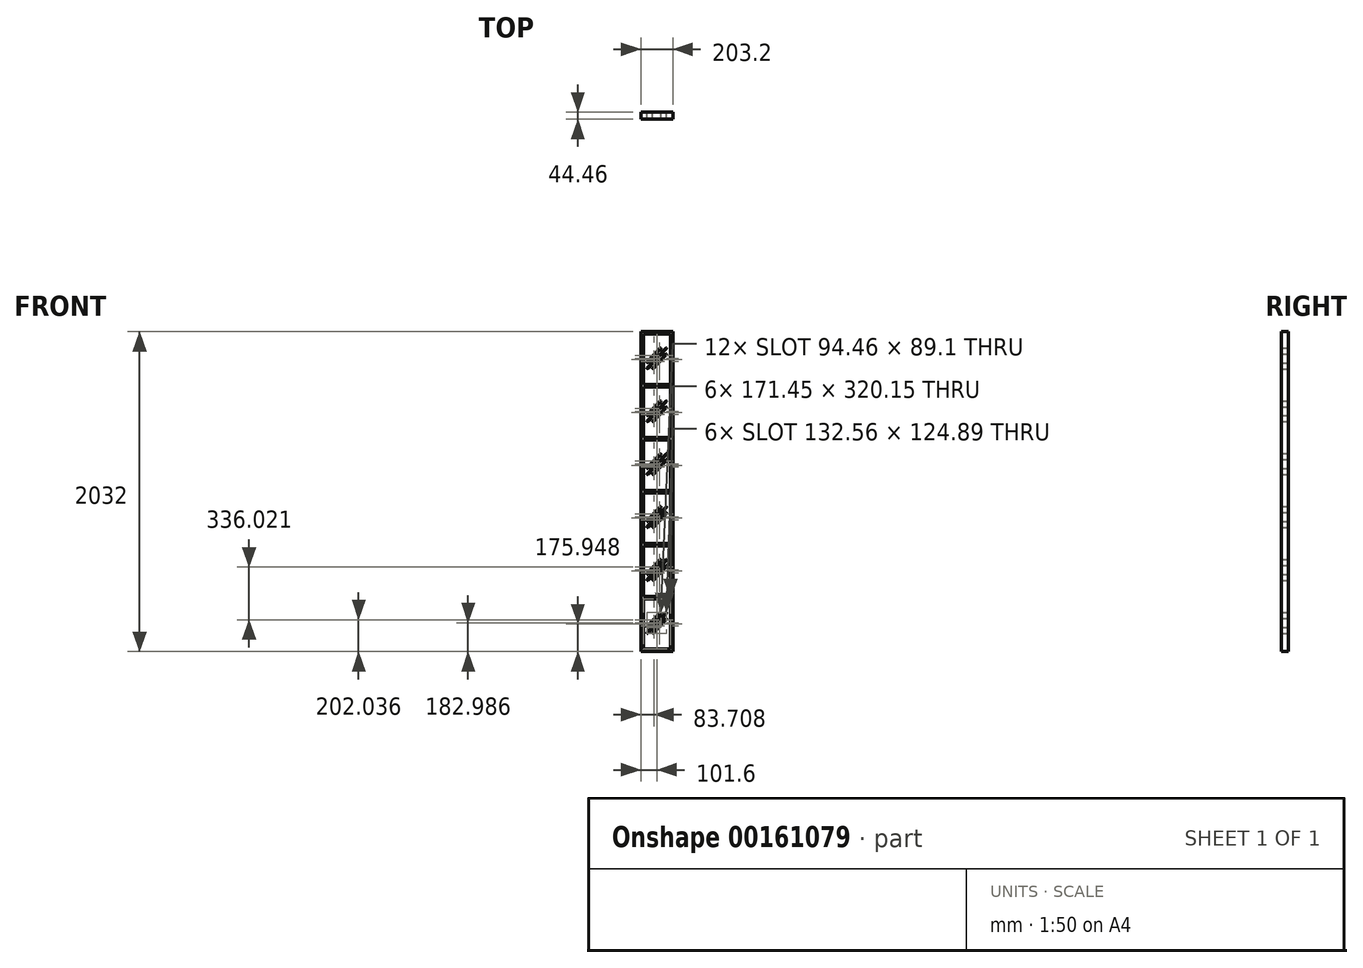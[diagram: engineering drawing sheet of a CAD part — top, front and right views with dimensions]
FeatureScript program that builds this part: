
annotation { "Feature Type Name" : "Feature", "Feature Type Description" : "" }
export const myFeature = defineFeature(function(context is Context, id is Id, definition is map)
    precondition{}
    {
        {
            var Q0;
            Q0=qCreatedBy(makeId("Front.planeOp"),FACE);
            var sketch = newSketch(context, id + "F0", { "sketchPlane" : qUnion([Q0])});
            skLineSegment(sketch, "E0.bottom", {"start": v(0, 0) * mm, "end": v(203.2, 0) * mm});
            skLineSegment(sketch, "E0.top", {"start": v(0, 2032) * mm, "end": v(203.2, 2032) * mm});
            skLineSegment(sketch, "E0.left", {"start": v(0, 0) * mm, "end": v(0, 2032) * mm});
            skLineSegment(sketch, "E0.right", {"start": v(203.2, 0) * mm, "end": v(203.2, 2032) * mm});
            skLineSegment(sketch, "E1.bottom", {"start": v(15.88, 15.88) * mm, "end": v(187.33, 15.88) * mm});
            skLineSegment(sketch, "E1.top", {"start": v(15.88, 336.02) * mm, "end": v(187.33, 336.02) * mm});
            skLineSegment(sketch, "E1.left", {"start": v(15.88, 15.88) * mm, "end": v(15.88, 336.02) * mm});
            skLineSegment(sketch, "E1.right", {"start": v(187.32, 15.88) * mm, "end": v(187.32, 336.02) * mm});
            skLineSegment(sketch, "E2.bottom", {"start": v(187.32, 351.9) * mm, "end": v(15.88, 351.9) * mm});
            skLineSegment(sketch, "E2.top", {"start": v(187.32, 672.04) * mm, "end": v(15.88, 672.04) * mm});
            skLineSegment(sketch, "E2.left", {"start": v(187.32, 351.9) * mm, "end": v(187.32, 672.04) * mm});
            skLineSegment(sketch, "E2.right", {"start": v(15.88, 351.9) * mm, "end": v(15.88, 672.04) * mm});
            skLineSegment(sketch, "E3.bottom", {"start": v(187.32, 687.92) * mm, "end": v(15.88, 687.92) * mm});
            skLineSegment(sketch, "E3.top", {"start": v(187.32, 1008.06) * mm, "end": v(15.88, 1008.06) * mm});
            skLineSegment(sketch, "E3.left", {"start": v(187.32, 687.92) * mm, "end": v(187.32, 1008.06) * mm});
            skLineSegment(sketch, "E3.right", {"start": v(15.88, 687.92) * mm, "end": v(15.87, 1008.06) * mm});
            skLineSegment(sketch, "E4.bottom", {"start": v(187.32, 1023.94) * mm, "end": v(15.88, 1023.94) * mm});
            skLineSegment(sketch, "E4.top", {"start": v(187.33, 1344.08) * mm, "end": v(15.87, 1344.08) * mm});
            skLineSegment(sketch, "E4.left", {"start": v(187.32, 1023.94) * mm, "end": v(187.32, 1344.08) * mm});
            skLineSegment(sketch, "E4.right", {"start": v(15.88, 1023.94) * mm, "end": v(15.87, 1344.08) * mm});
            skLineSegment(sketch, "E5.bottom", {"start": v(187.33, 1359.96) * mm, "end": v(15.87, 1359.96) * mm});
            skLineSegment(sketch, "E5.top", {"start": v(187.32, 1680.1) * mm, "end": v(15.87, 1680.1) * mm});
            skLineSegment(sketch, "E5.left", {"start": v(187.32, 1359.96) * mm, "end": v(187.32, 1680.1) * mm});
            skLineSegment(sketch, "E5.right", {"start": v(15.87, 1359.96) * mm, "end": v(15.87, 1680.1) * mm});
            skLineSegment(sketch, "E6.bottom", {"start": v(187.33, 1695.98) * mm, "end": v(15.87, 1695.98) * mm});
            skLineSegment(sketch, "E6.top", {"start": v(187.33, 2016.13) * mm, "end": v(15.87, 2016.13) * mm});
            skLineSegment(sketch, "E6.left", {"start": v(187.32, 1695.98) * mm, "end": v(187.32, 2016.13) * mm});
            skLineSegment(sketch, "E6.right", {"start": v(15.87, 1695.98) * mm, "end": v(15.87, 2016.13) * mm});
            skSolve(sketch);
        }
        {
            var Q0;
            Q0=qSketchRegion(id+"F0",true);
            extrude(context, id + "F1", {"entities" : qUnion([Q0]), "depth" : 22.22 * mm, "hasSecondDirection" : true, "secondDirectionOppositeDirection" : true, "secondDirectionDepth" : 22.22 * mm});
        }
        {
            var Q0;
            Q0=qCreatedBy(makeId("Front.planeOp"),FACE);
            var sketch = newSketch(context, id + "F2", { "sketchPlane" : qUnion([Q0])});
            skLineSegment(sketch, "E7.0", {"start": v(187.32, 1680.1) * mm, "end": v(15.87, 1680.1) * mm});
            skLineSegment(sketch, "E8.0", {"start": v(15.87, 1359.96) * mm, "end": v(15.87, 1680.1) * mm});
            skLineSegment(sketch, "E9.0", {"start": v(187.32, 1359.96) * mm, "end": v(15.87, 1359.96) * mm});
            skLineSegment(sketch, "E10.0", {"start": v(187.32, 1359.96) * mm, "end": v(187.32, 1680.1) * mm});
            skLineSegment(sketch, "E11.0", {"start": v(187.32, 1023.94) * mm, "end": v(187.32, 1344.08) * mm});
            skLineSegment(sketch, "E12.0", {"start": v(187.32, 1344.08) * mm, "end": v(15.87, 1344.08) * mm});
            skLineSegment(sketch, "E13.0", {"start": v(15.88, 1023.94) * mm, "end": v(15.87, 1344.08) * mm});
            skLineSegment(sketch, "E14.0", {"start": v(187.32, 1023.94) * mm, "end": v(15.88, 1023.94) * mm});
            skLineSegment(sketch, "E15.0", {"start": v(187.32, 1008.06) * mm, "end": v(15.88, 1008.06) * mm});
            skLineSegment(sketch, "E16.0", {"start": v(15.88, 687.92) * mm, "end": v(15.87, 1008.06) * mm});
            skLineSegment(sketch, "E17.0", {"start": v(187.32, 687.92) * mm, "end": v(187.32, 1008.06) * mm});
            skLineSegment(sketch, "E18.0", {"start": v(187.32, 687.92) * mm, "end": v(15.88, 687.92) * mm});
            skLineSegment(sketch, "E19.0", {"start": v(187.32, 351.9) * mm, "end": v(187.32, 672.04) * mm});
            skLineSegment(sketch, "E20.0", {"start": v(187.32, 351.9) * mm, "end": v(15.88, 351.9) * mm});
            skLineSegment(sketch, "E21.0", {"start": v(187.32, 672.04) * mm, "end": v(15.88, 672.04) * mm});
            skLineSegment(sketch, "E22.0", {"start": v(15.88, 351.9) * mm, "end": v(15.88, 672.04) * mm});
            skLineSegment(sketch, "E23.0", {"start": v(15.88, 336.02) * mm, "end": v(187.32, 336.02) * mm});
            skLineSegment(sketch, "E24.0", {"start": v(15.88, 15.88) * mm, "end": v(15.88, 336.02) * mm});
            skLineSegment(sketch, "E25.0", {"start": v(187.32, 15.88) * mm, "end": v(187.32, 336.02) * mm});
            skLineSegment(sketch, "E26.0", {"start": v(15.88, 15.88) * mm, "end": v(187.32, 15.88) * mm});
            skLineSegment(sketch, "E27", {"start": v(160.87, 246.1) * mm, "end": v(42.33, 119.88) * mm});
            skLineSegment(sketch, "E28", {"start": v(160.87, 208) * mm, "end": v(78.11, 119.88) * mm});
            skLineSegment(sketch, "E29", {"start": v(125.09, 246.1) * mm, "end": v(42.33, 157.98) * mm});
            skArc(sketch, "E30.0.startCap", {"start": v(122.77, 248.27) * mm, "mid": v(127.26, 248.4) * mm, "end": v(127.4, 243.92) * mm});
            skArc(sketch, "E30.0.endCap", {"start": v(44.64, 155.8) * mm, "mid": v(40.16, 155.67) * mm, "end": v(40.01, 160.15) * mm});
            skLineSegment(sketch, "E30.0.left", {"start": v(127.4, 243.92) * mm, "end": v(44.64, 155.8) * mm});
            skLineSegment(sketch, "E30.0.right", {"start": v(122.77, 248.27) * mm, "end": v(40.01, 160.15) * mm});
            skArc(sketch, "E30.1.startCap", {"start": v(158.56, 248.27) * mm, "mid": v(163.04, 248.4) * mm, "end": v(163.19, 243.92) * mm});
            skArc(sketch, "E30.1.endCap", {"start": v(44.64, 117.7) * mm, "mid": v(40.16, 117.57) * mm, "end": v(40.01, 122.05) * mm});
            skLineSegment(sketch, "E30.1.left", {"start": v(163.19, 243.92) * mm, "end": v(44.64, 117.7) * mm});
            skLineSegment(sketch, "E30.1.right", {"start": v(158.56, 248.27) * mm, "end": v(40.01, 122.05) * mm});
            skArc(sketch, "E30.2.startCap", {"start": v(158.56, 210.17) * mm, "mid": v(163.04, 210.3) * mm, "end": v(163.19, 205.82) * mm});
            skArc(sketch, "E30.2.endCap", {"start": v(80.43, 117.7) * mm, "mid": v(75.94, 117.57) * mm, "end": v(75.8, 122.05) * mm});
            skLineSegment(sketch, "E30.2.left", {"start": v(163.19, 205.82) * mm, "end": v(80.43, 117.7) * mm});
            skLineSegment(sketch, "E30.2.right", {"start": v(158.56, 210.17) * mm, "end": v(75.8, 122.05) * mm});
            skLineSegment(sketch, "E31.0.1.0", {"start": v(160.87, 582.11) * mm, "end": v(42.33, 455.9) * mm});
            skLineSegment(sketch, "E31.0.1.1", {"start": v(158.56, 546.19) * mm, "end": v(75.8, 458.07) * mm});
            skLineSegment(sketch, "E31.0.1.2", {"start": v(163.19, 579.94) * mm, "end": v(44.64, 453.73) * mm});
            skLineSegment(sketch, "E31.0.1.3", {"start": v(122.77, 584.29) * mm, "end": v(40.01, 496.17) * mm});
            skLineSegment(sketch, "E31.0.1.4", {"start": v(163.19, 541.84) * mm, "end": v(80.43, 453.73) * mm});
            skLineSegment(sketch, "E31.0.1.5", {"start": v(127.4, 579.94) * mm, "end": v(44.64, 491.83) * mm});
            skLineSegment(sketch, "E31.0.1.6", {"start": v(160.87, 544.01) * mm, "end": v(78.11, 455.9) * mm});
            skLineSegment(sketch, "E31.0.1.7", {"start": v(125.09, 582.11) * mm, "end": v(42.33, 494) * mm});
            skLineSegment(sketch, "E31.0.1.8", {"start": v(158.56, 584.29) * mm, "end": v(40.01, 458.07) * mm});
            skArc(sketch, "E31.0.1.9", {"start": v(122.77, 584.29) * mm, "mid": v(127.26, 584.43) * mm, "end": v(127.4, 579.94) * mm});
            skArc(sketch, "E31.0.1.10", {"start": v(158.56, 584.29) * mm, "mid": v(163.04, 584.43) * mm, "end": v(163.19, 579.94) * mm});
            skArc(sketch, "E31.0.1.11", {"start": v(44.64, 453.73) * mm, "mid": v(40.16, 453.59) * mm, "end": v(40.01, 458.07) * mm});
            skArc(sketch, "E31.0.1.12", {"start": v(44.64, 491.83) * mm, "mid": v(40.16, 491.69) * mm, "end": v(40.01, 496.17) * mm});
            skArc(sketch, "E31.0.1.13", {"start": v(80.43, 453.73) * mm, "mid": v(75.94, 453.59) * mm, "end": v(75.8, 458.07) * mm});
            skArc(sketch, "E31.0.1.14", {"start": v(158.56, 546.19) * mm, "mid": v(163.04, 546.33) * mm, "end": v(163.19, 541.84) * mm});
            skLineSegment(sketch, "E31.0.2.0", {"start": v(160.87, 918.13) * mm, "end": v(42.33, 791.92) * mm});
            skLineSegment(sketch, "E31.0.2.1", {"start": v(158.56, 882.2) * mm, "end": v(75.8, 794.1) * mm});
            skLineSegment(sketch, "E31.0.2.2", {"start": v(163.19, 915.96) * mm, "end": v(44.64, 789.75) * mm});
            skLineSegment(sketch, "E31.0.2.3", {"start": v(122.77, 920.3) * mm, "end": v(40.01, 832.2) * mm});
            skLineSegment(sketch, "E31.0.2.4", {"start": v(163.19, 877.86) * mm, "end": v(80.43, 789.75) * mm});
            skLineSegment(sketch, "E31.0.2.5", {"start": v(127.4, 915.96) * mm, "end": v(44.64, 827.85) * mm});
            skLineSegment(sketch, "E31.0.2.6", {"start": v(160.87, 880.03) * mm, "end": v(78.11, 791.92) * mm});
            skLineSegment(sketch, "E31.0.2.7", {"start": v(125.09, 918.13) * mm, "end": v(42.33, 830.02) * mm});
            skLineSegment(sketch, "E31.0.2.8", {"start": v(158.56, 920.3) * mm, "end": v(40.01, 794.1) * mm});
            skArc(sketch, "E31.0.2.9", {"start": v(122.77, 920.3) * mm, "mid": v(127.26, 920.45) * mm, "end": v(127.4, 915.96) * mm});
            skArc(sketch, "E31.0.2.10", {"start": v(158.56, 920.3) * mm, "mid": v(163.04, 920.45) * mm, "end": v(163.19, 915.96) * mm});
            skArc(sketch, "E31.0.2.11", {"start": v(44.64, 789.75) * mm, "mid": v(40.16, 789.6) * mm, "end": v(40.01, 794.1) * mm});
            skArc(sketch, "E31.0.2.12", {"start": v(44.64, 827.85) * mm, "mid": v(40.16, 827.7) * mm, "end": v(40.01, 832.2) * mm});
            skArc(sketch, "E31.0.2.13", {"start": v(80.43, 789.75) * mm, "mid": v(75.94, 789.6) * mm, "end": v(75.8, 794.1) * mm});
            skArc(sketch, "E31.0.2.14", {"start": v(158.56, 882.2) * mm, "mid": v(163.04, 882.35) * mm, "end": v(163.19, 877.86) * mm});
            skLineSegment(sketch, "E31.0.3.0", {"start": v(160.87, 1254.15) * mm, "end": v(42.33, 1127.94) * mm});
            skLineSegment(sketch, "E31.0.3.1", {"start": v(158.56, 1218.23) * mm, "end": v(75.8, 1130.12) * mm});
            skLineSegment(sketch, "E31.0.3.2", {"start": v(163.19, 1251.98) * mm, "end": v(44.64, 1125.77) * mm});
            skLineSegment(sketch, "E31.0.3.3", {"start": v(122.77, 1256.33) * mm, "end": v(40.01, 1168.22) * mm});
            skLineSegment(sketch, "E31.0.3.4", {"start": v(163.19, 1213.88) * mm, "end": v(80.43, 1125.77) * mm});
            skLineSegment(sketch, "E31.0.3.5", {"start": v(127.4, 1251.98) * mm, "end": v(44.64, 1163.87) * mm});
            skLineSegment(sketch, "E31.0.3.6", {"start": v(160.87, 1216.05) * mm, "end": v(78.11, 1127.94) * mm});
            skLineSegment(sketch, "E31.0.3.7", {"start": v(125.09, 1254.15) * mm, "end": v(42.33, 1166.04) * mm});
            skLineSegment(sketch, "E31.0.3.8", {"start": v(158.56, 1256.33) * mm, "end": v(40.01, 1130.12) * mm});
            skArc(sketch, "E31.0.3.9", {"start": v(122.77, 1256.33) * mm, "mid": v(127.26, 1256.47) * mm, "end": v(127.4, 1251.98) * mm});
            skArc(sketch, "E31.0.3.10", {"start": v(158.56, 1256.33) * mm, "mid": v(163.04, 1256.47) * mm, "end": v(163.19, 1251.98) * mm});
            skArc(sketch, "E31.0.3.11", {"start": v(44.64, 1125.77) * mm, "mid": v(40.16, 1125.63) * mm, "end": v(40.01, 1130.12) * mm});
            skArc(sketch, "E31.0.3.12", {"start": v(44.64, 1163.87) * mm, "mid": v(40.16, 1163.73) * mm, "end": v(40.01, 1168.22) * mm});
            skArc(sketch, "E31.0.3.13", {"start": v(80.43, 1125.77) * mm, "mid": v(75.94, 1125.63) * mm, "end": v(75.8, 1130.12) * mm});
            skArc(sketch, "E31.0.3.14", {"start": v(158.56, 1218.23) * mm, "mid": v(163.04, 1218.37) * mm, "end": v(163.19, 1213.88) * mm});
            skLineSegment(sketch, "E31.0.4.0", {"start": v(160.87, 1590.18) * mm, "end": v(42.33, 1463.96) * mm});
            skLineSegment(sketch, "E31.0.4.1", {"start": v(158.56, 1554.25) * mm, "end": v(75.8, 1466.14) * mm});
            skLineSegment(sketch, "E31.0.4.2", {"start": v(163.19, 1588) * mm, "end": v(44.64, 1461.79) * mm});
            skLineSegment(sketch, "E31.0.4.3", {"start": v(122.77, 1592.35) * mm, "end": v(40.01, 1504.24) * mm});
            skLineSegment(sketch, "E31.0.4.4", {"start": v(163.19, 1549.9) * mm, "end": v(80.43, 1461.79) * mm});
            skLineSegment(sketch, "E31.0.4.5", {"start": v(127.4, 1588) * mm, "end": v(44.64, 1499.89) * mm});
            skLineSegment(sketch, "E31.0.4.6", {"start": v(160.87, 1552.08) * mm, "end": v(78.11, 1463.96) * mm});
            skLineSegment(sketch, "E31.0.4.7", {"start": v(125.09, 1590.18) * mm, "end": v(42.33, 1502.06) * mm});
            skLineSegment(sketch, "E31.0.4.8", {"start": v(158.56, 1592.35) * mm, "end": v(40.01, 1466.14) * mm});
            skArc(sketch, "E31.0.4.9", {"start": v(122.77, 1592.35) * mm, "mid": v(127.26, 1592.49) * mm, "end": v(127.4, 1588) * mm});
            skArc(sketch, "E31.0.4.10", {"start": v(158.56, 1592.35) * mm, "mid": v(163.04, 1592.49) * mm, "end": v(163.19, 1588) * mm});
            skArc(sketch, "E31.0.4.11", {"start": v(44.64, 1461.79) * mm, "mid": v(40.16, 1461.65) * mm, "end": v(40.01, 1466.14) * mm});
            skArc(sketch, "E31.0.4.12", {"start": v(44.64, 1499.89) * mm, "mid": v(40.16, 1499.75) * mm, "end": v(40.01, 1504.24) * mm});
            skArc(sketch, "E31.0.4.13", {"start": v(80.43, 1461.79) * mm, "mid": v(75.94, 1461.65) * mm, "end": v(75.8, 1466.14) * mm});
            skArc(sketch, "E31.0.4.14", {"start": v(158.56, 1554.25) * mm, "mid": v(163.04, 1554.39) * mm, "end": v(163.19, 1549.9) * mm});
            skLineSegment(sketch, "E31.direction1", {"start": v(40.01, 122.05) * mm, "end": v(311.48, 122.05) * mm, "construction": true});
            skLineSegment(sketch, "E31.direction2", {"start": v(40.01, 122.05) * mm, "end": v(40.01, 458.07) * mm, "construction": true});
            skLineSegment(sketch, "E32.0", {"start": v(187.32, 2016.13) * mm, "end": v(15.87, 2016.13) * mm});
            skLineSegment(sketch, "E33.0", {"start": v(15.87, 1695.98) * mm, "end": v(15.87, 2016.13) * mm});
            skLineSegment(sketch, "E34.0", {"start": v(187.32, 1695.98) * mm, "end": v(15.87, 1695.98) * mm});
            skLineSegment(sketch, "E35.0", {"start": v(187.32, 1695.98) * mm, "end": v(187.32, 2016.13) * mm});
            skLineSegment(sketch, "E36.0.0.5", {"start": v(160.87, 1926.2) * mm, "end": v(42.33, 1799.98) * mm});
            skLineSegment(sketch, "E36.3.0.5", {"start": v(158.56, 1890.27) * mm, "end": v(75.8, 1802.16) * mm});
            skLineSegment(sketch, "E36.6.0.5", {"start": v(163.19, 1924.02) * mm, "end": v(44.64, 1797.81) * mm});
            skLineSegment(sketch, "E36.9.0.5", {"start": v(122.77, 1928.37) * mm, "end": v(40.01, 1840.26) * mm});
            skLineSegment(sketch, "E36.12.0.5", {"start": v(163.19, 1885.92) * mm, "end": v(80.43, 1797.81) * mm});
            skLineSegment(sketch, "E36.15.0.5", {"start": v(127.4, 1924.02) * mm, "end": v(44.64, 1835.91) * mm});
            skLineSegment(sketch, "E36.18.0.5", {"start": v(160.87, 1888.1) * mm, "end": v(78.11, 1799.98) * mm});
            skLineSegment(sketch, "E36.21.0.5", {"start": v(125.09, 1926.2) * mm, "end": v(42.33, 1838.08) * mm});
            skLineSegment(sketch, "E36.24.0.5", {"start": v(158.56, 1928.37) * mm, "end": v(40.01, 1802.16) * mm});
            skArc(sketch, "E36.27.0.5", {"start": v(122.77, 1928.37) * mm, "mid": v(127.26, 1928.51) * mm, "end": v(127.4, 1924.02) * mm});
            skArc(sketch, "E36.31.0.5", {"start": v(158.56, 1928.37) * mm, "mid": v(163.04, 1928.51) * mm, "end": v(163.19, 1924.02) * mm});
            skArc(sketch, "E36.35.0.5", {"start": v(44.64, 1797.81) * mm, "mid": v(40.16, 1797.67) * mm, "end": v(40.01, 1802.16) * mm});
            skArc(sketch, "E36.39.0.5", {"start": v(44.64, 1835.91) * mm, "mid": v(40.16, 1835.77) * mm, "end": v(40.01, 1840.26) * mm});
            skArc(sketch, "E36.43.0.5", {"start": v(80.43, 1797.81) * mm, "mid": v(75.94, 1797.67) * mm, "end": v(75.8, 1802.16) * mm});
            skArc(sketch, "E36.47.0.5", {"start": v(158.56, 1890.27) * mm, "mid": v(163.04, 1890.41) * mm, "end": v(163.19, 1885.92) * mm});
            skLineSegment(sketch, "E37", {"start": v(160.87, 246.1) * mm, "end": v(187.32, 246.1) * mm});
            skSolve(sketch);
        }
        {
            var Q0;
            Q0=qSketchRegion(id+"F2",true);
            extrude(context, id + "F3", {"entities" : qUnion([Q0]), "operationType" : NewBodyOperationType.ADD, "depth" : 21.59 * mm, "hasSecondDirection" : true, "secondDirectionOppositeDirection" : true, "secondDirectionDepth" : 21.59 * mm});
        }
    });
